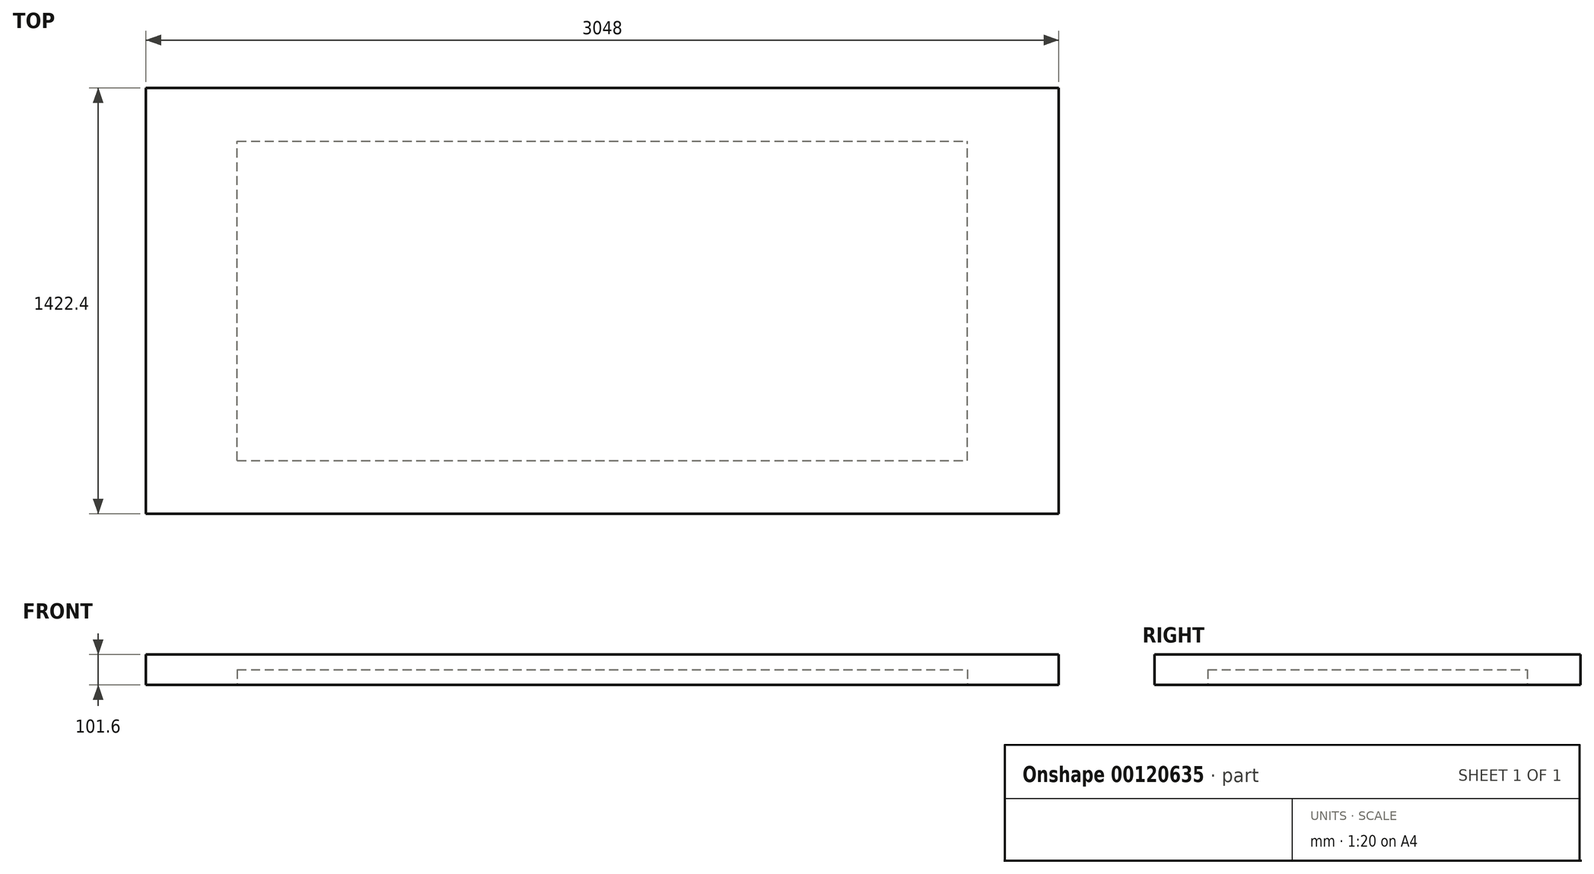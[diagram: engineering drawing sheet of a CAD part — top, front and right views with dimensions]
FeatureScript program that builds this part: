
annotation { "Feature Type Name" : "Feature", "Feature Type Description" : "" }
export const myFeature = defineFeature(function(context is Context, id is Id, definition is map)
    precondition{}
    {
        {
            var Q0;
            Q0=qCreatedBy(makeId("Top.planeOp"),FACE);
            var sketch = newSketch(context, id + "F0", { "sketchPlane" : qUnion([Q0])});
            skLineSegment(sketch, "E0.bottom", {"start": v(-1524, 711.2) * mm, "end": v(1524, 711.2) * mm});
            skLineSegment(sketch, "E0.top", {"start": v(-1524, -711.2) * mm, "end": v(1524, -711.2) * mm});
            skLineSegment(sketch, "E0.left", {"start": v(-1524, 711.2) * mm, "end": v(-1524, -711.2) * mm});
            skLineSegment(sketch, "E0.right", {"start": v(1524, 711.2) * mm, "end": v(1524, -711.2) * mm});
            skPoint(sketch, "E0.middle", {"position": v(0, 0) * mm});
            skSolve(sketch);
        }
        {
            var Q0;
            Q0=qSketchRegion(id+"F0",true);
            extrude(context, id + "F1", {"entities" : qUnion([Q0]), "depth" : 101.6 * mm});
        }
        {
            var Q0;
            Q0=makeQuery(id+"F1.opExtrude","CAP_FACE",FACE,{"disambiguationData":[OSD([sQuery(id+"F0.wireOp",EDGE,"E0.bottom"),sQuery(id+"F0.wireOp",EDGE,"E0.top"),sQuery(id+"F0.wireOp",EDGE,"E0.left"),sQuery(id+"F0.wireOp",EDGE,"E0.right")])],"isStart":true});
            var sketch = newSketch(context, id + "F2", { "sketchPlane" : qUnion([Q0])});
            skLineSegment(sketch, "E1.bottom", {"start": v(-1219.2, 533.4) * mm, "end": v(1219.2, 533.4) * mm});
            skLineSegment(sketch, "E1.top", {"start": v(-1219.2, -533.4) * mm, "end": v(1219.2, -533.4) * mm});
            skLineSegment(sketch, "E1.left", {"start": v(-1219.2, 533.4) * mm, "end": v(-1219.2, -533.4) * mm});
            skLineSegment(sketch, "E1.right", {"start": v(1219.2, 533.4) * mm, "end": v(1219.2, -533.4) * mm});
            skPoint(sketch, "E1.middle", {"position": v(0, 0) * mm});
            skSolve(sketch);
        }
        {
            var Q0;
            Q0 = qSketchRegion(id + "F2", true);
            extrude(context, id + "F3", {"entities" : qUnion([Q0]), "operationType" : NewBodyOperationType.REMOVE, "oppositeDirection" : true, "depth" : 50.8 * mm});
        }
    });
